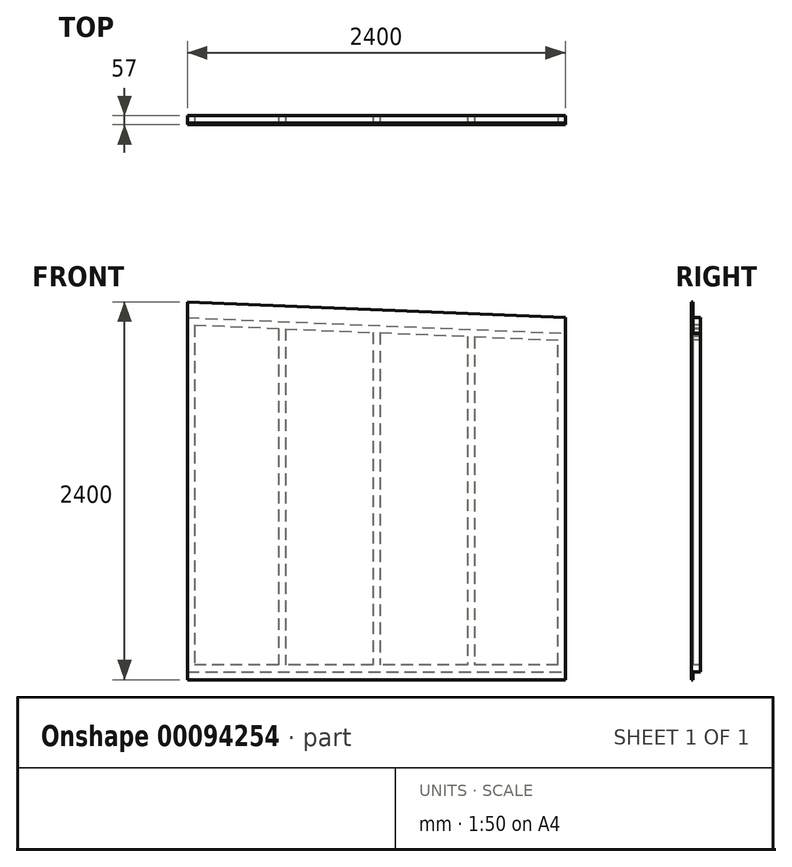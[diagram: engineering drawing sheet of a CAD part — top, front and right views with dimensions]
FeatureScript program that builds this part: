
annotation { "Feature Type Name" : "Feature", "Feature Type Description" : "" }
export const myFeature = defineFeature(function(context is Context, id is Id, definition is map)
    precondition{}
    {
        {
            var Q0;
            Q0=qCreatedBy(makeId("Front.planeOp"),FACE);
            var sketch = newSketch(context, id + "F0", { "sketchPlane" : qUnion([Q0])});
            skLineSegment(sketch, "E0.bottom", {"start": v(1200, -1175) * mm, "end": v(-1200, -1175) * mm});
            skLineSegment(sketch, "E0.left", {"start": v(1200, -1175) * mm, "end": v(1200, 1125) * mm});
            skLineSegment(sketch, "E0.right", {"start": v(-1200, -1175) * mm, "end": v(-1200, 1225) * mm});
            skLineSegment(sketch, "E1", {"start": v(-1200, 1225) * mm, "end": v(1200, 1125) * mm});
            skLineSegment(sketch, "E2", {"start": v(-1200, 1125) * mm, "end": v(1200, 1025) * mm});
            skLineSegment(sketch, "E3", {"start": v(-1200, 1079.96) * mm, "end": v(1200, 979.96) * mm});
            skLineSegment(sketch, "E4", {"start": v(-1200, -1125) * mm, "end": v(1200, -1125) * mm});
            skLineSegment(sketch, "E5", {"start": v(1200, -1080) * mm, "end": v(-1200, -1080) * mm});
            skLineSegment(sketch, "E6", {"start": v(1155, -1080) * mm, "end": v(1155, 981.84) * mm});
            skLineSegment(sketch, "E7", {"start": v(-1155, 1078.09) * mm, "end": v(-1155, -1080) * mm});
            skLineSegment(sketch, "E8", {"start": v(-600, -1080) * mm, "end": v(-600, 1258.53) * mm, "construction": true});
            skLineSegment(sketch, "E9", {"start": v(0, 1332.7) * mm, "end": v(0, -1314.56) * mm, "construction": true});
            skLineSegment(sketch, "E10", {"start": v(600, 1290.83) * mm, "end": v(600, -1080) * mm, "construction": true});
            skLineSegment(sketch, "E11", {"start": v(-622.5, 1055.9) * mm, "end": v(-622.5, -1080) * mm});
            skLineSegment(sketch, "E12", {"start": v(-22.5, 1030.9) * mm, "end": v(-22.5, -1080) * mm});
            skLineSegment(sketch, "E13.MirrorCS", {"start": v(622.5, 1004.02) * mm, "end": v(622.5, -1080) * mm});
            skLineSegment(sketch, "E14.trimOffspring", {"start": v(-577.5, 1054.02) * mm, "end": v(-577.5, -1080) * mm});
            skPoint(sketch, "E15.MirrorCS.start.orphan", {"position": v(-577.5, 1258.61) * mm});
            skPoint(sketch, "E16.orphan", {"position": v(-622.5, 1258.61) * mm});
            skLineSegment(sketch, "E17.trimOffspring", {"start": v(22.5, 1029.02) * mm, "end": v(22.5, -1080) * mm});
            skPoint(sketch, "E18.MirrorCS.start.orphan", {"position": v(22.5, 1253.07) * mm});
            skPoint(sketch, "E19.orphan", {"position": v(-22.5, 1253.07) * mm});
            skLineSegment(sketch, "E20.trimOffspring", {"start": v(577.5, 1005.9) * mm, "end": v(577.5, -1080) * mm});
            skPoint(sketch, "E21.MirrorCS.start.orphan", {"position": v(577.5, 1258.61) * mm});
            skPoint(sketch, "E22.orphan", {"position": v(622.5, 1258.61) * mm});
            skSolve(sketch);
        }
        {
            var Q0;
            {var subQ3=sQuery(id+"F0.wireOp",EDGE,"E2");Q0=makeQuery(id+"F0.imprint","IMPRINT",FACE,{"disambiguationData":[TD([[makeQuery(id+"F0.imprint","IMPRINT",EDGE,{"derivedFrom":subQ3}),-1.0]])]});}
            var Q1;
            {var subQ5=sQuery(id+"F0.wireOp",EDGE,"E7");Q1=makeQuery(id+"F0.imprint","IMPRINT",FACE,{"disambiguationData":[TD([[makeQuery(id+"F0.imprint","IMPRINT",EDGE,{"derivedFrom":subQ5}),-1.0]])]});}
            var Q2;
            {var subQ0=sQuery(id+"F0.wireOp",EDGE,"E11");Q2=makeQuery(id+"F0.imprint","IMPRINT",FACE,{"disambiguationData":[TD([[makeQuery(id+"F0.imprint","IMPRINT",EDGE,{"derivedFrom":subQ0}),1.0]])]});}
            var Q3;
            {var subQ0=sQuery(id+"F0.wireOp",EDGE,"E12");Q3=makeQuery(id+"F0.imprint","IMPRINT",FACE,{"disambiguationData":[TD([[makeQuery(id+"F0.imprint","IMPRINT",EDGE,{"derivedFrom":subQ0}),1.0]])]});}
            var Q4;
            {var subQ0=sQuery(id+"F0.wireOp",EDGE,"E13.MirrorCS");Q4=makeQuery(id+"F0.imprint","IMPRINT",FACE,{"disambiguationData":[TD([[makeQuery(id+"F0.imprint","IMPRINT",EDGE,{"derivedFrom":subQ0}),-1.0]])]});}
            var Q5;
            {var subQ5=sQuery(id+"F0.wireOp",EDGE,"E6");Q5=makeQuery(id+"F0.imprint","IMPRINT",FACE,{"disambiguationData":[TD([[makeQuery(id+"F0.imprint","IMPRINT",EDGE,{"derivedFrom":subQ5}),-1.0]])]});}
            var Q6;
            {var subQ12=sQuery(id+"F0.wireOp",EDGE,"E4");Q6=makeQuery(id+"F0.imprint","IMPRINT",FACE,{"disambiguationData":[TD([[makeQuery(id+"F0.imprint","IMPRINT",EDGE,{"derivedFrom":subQ12}),1.0]])]});}
            extrude(context, id + "F1", {"entities" : qUnion([Q0, Q1, Q2, Q3, Q4, Q5, Q6]), "oppositeDirection" : true, "depth" : 45 * mm});
        }
        {
            var Q0;
            {var subQ0=sQuery(id+"F0.wireOp",EDGE,"E7");Q0=makeQuery(id+"F0.imprint","IMPRINT",FACE,{"disambiguationData":[TD([[makeQuery(id+"F0.imprint","IMPRINT",EDGE,{"derivedFrom":subQ0}),1.0]])]});}
            var Q1;
            {var subQ0=sQuery(id+"F0.wireOp",EDGE,"E12");Q1=makeQuery(id+"F0.imprint","IMPRINT",FACE,{"disambiguationData":[TD([[makeQuery(id+"F0.imprint","IMPRINT",EDGE,{"derivedFrom":subQ0}),-1.0]])]});}
            var Q2;
            {var subQ0=sQuery(id+"F0.wireOp",EDGE,"E17.trimOffspring");Q2=makeQuery(id+"F0.imprint","IMPRINT",FACE,{"disambiguationData":[TD([[makeQuery(id+"F0.imprint","IMPRINT",EDGE,{"derivedFrom":subQ0}),1.0]])]});}
            var Q3;
            {var subQ0=sQuery(id+"F0.wireOp",EDGE,"E6");Q3=makeQuery(id+"F0.imprint","IMPRINT",FACE,{"disambiguationData":[TD([[makeQuery(id+"F0.imprint","IMPRINT",EDGE,{"derivedFrom":subQ0}),1.0]])]});}
            var Q4;
            {var subQ0=sQuery(id+"F0.wireOp",EDGE,"E1");Q4=makeQuery(id+"F0.imprint","IMPRINT",FACE,{"disambiguationData":[TD([[makeQuery(id+"F0.imprint","IMPRINT",EDGE,{"derivedFrom":subQ0}),-1.0]])]});}
            var Q5;
            {var subQ3=sQuery(id+"F0.wireOp",EDGE,"E2");Q5=makeQuery(id+"F0.imprint","IMPRINT",FACE,{"disambiguationData":[TD([[makeQuery(id+"F0.imprint","IMPRINT",EDGE,{"derivedFrom":subQ3}),-1.0]])]});}
            var Q6;
            {var subQ5=sQuery(id+"F0.wireOp",EDGE,"E7");Q6=makeQuery(id+"F0.imprint","IMPRINT",FACE,{"disambiguationData":[TD([[makeQuery(id+"F0.imprint","IMPRINT",EDGE,{"derivedFrom":subQ5}),-1.0]])]});}
            var Q7;
            {var subQ0=sQuery(id+"F0.wireOp",EDGE,"E11");Q7=makeQuery(id+"F0.imprint","IMPRINT",FACE,{"disambiguationData":[TD([[makeQuery(id+"F0.imprint","IMPRINT",EDGE,{"derivedFrom":subQ0}),1.0]])]});}
            var Q8;
            {var subQ0=sQuery(id+"F0.wireOp",EDGE,"E12");Q8=makeQuery(id+"F0.imprint","IMPRINT",FACE,{"disambiguationData":[TD([[makeQuery(id+"F0.imprint","IMPRINT",EDGE,{"derivedFrom":subQ0}),1.0]])]});}
            var Q9;
            {var subQ0=sQuery(id+"F0.wireOp",EDGE,"E13.MirrorCS");Q9=makeQuery(id+"F0.imprint","IMPRINT",FACE,{"disambiguationData":[TD([[makeQuery(id+"F0.imprint","IMPRINT",EDGE,{"derivedFrom":subQ0}),-1.0]])]});}
            var Q10;
            {var subQ5=sQuery(id+"F0.wireOp",EDGE,"E6");Q10=makeQuery(id+"F0.imprint","IMPRINT",FACE,{"disambiguationData":[TD([[makeQuery(id+"F0.imprint","IMPRINT",EDGE,{"derivedFrom":subQ5}),-1.0]])]});}
            var Q11;
            {var subQ12=sQuery(id+"F0.wireOp",EDGE,"E4");Q11=makeQuery(id+"F0.imprint","IMPRINT",FACE,{"disambiguationData":[TD([[makeQuery(id+"F0.imprint","IMPRINT",EDGE,{"derivedFrom":subQ12}),1.0]])]});}
            var Q12;
            {var subQ0=sQuery(id+"F0.wireOp",EDGE,"E0.bottom");Q12=makeQuery(id+"F0.imprint","IMPRINT",FACE,{"disambiguationData":[TD([[makeQuery(id+"F0.imprint","IMPRINT",EDGE,{"derivedFrom":subQ0}),-1.0]])]});}
            extrude(context, id + "F2", {"entities" : qUnion([Q0, Q1, Q2, Q3, Q4, Q5, Q6, Q7, Q8, Q9, Q10, Q11, Q12]), "operationType" : NewBodyOperationType.ADD, "depth" : 12 * mm});
        }
    });
